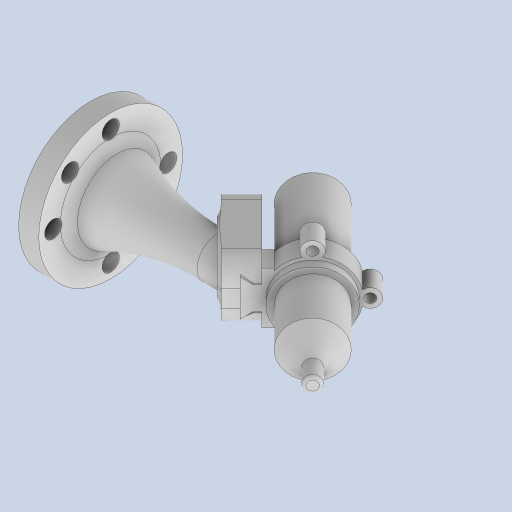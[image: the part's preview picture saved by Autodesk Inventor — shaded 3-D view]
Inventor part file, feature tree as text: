
AUTODESK INVENTOR PART (.ipt)
format: ipt  version: 2024 (Build 280153000, 153)  size: 855,552 bytes
history: native  units: mm
features: other x7, sketch x2
ambient origin geometry x8: Origin, YZ Plane, XZ Plane, XY Plane, X Axis, Y Axis, Z Axis, Center Point
bodies: Body1 (feature_tree)
feature tree (9):
  other  "TCP_Final.iam"
  other  "acople_v2.ipt:1"
  other  "Porta herramientas p1.ipt:1"
  other  "Porta herramientas p2.ipt:1"
  other  "Marcador_V2.ipt:1"
  other  "Sólido2"
  sketch  "Sketch2"  dims[d1=10.0mm]
  sketch  "Sketch4"
  other  "Work Axis1"
